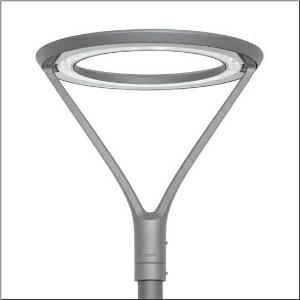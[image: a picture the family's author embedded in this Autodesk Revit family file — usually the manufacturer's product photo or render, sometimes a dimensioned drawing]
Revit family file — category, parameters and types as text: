
# Revit family: dl_r__20___pl1_2s_5xa512832s008_323f
name_source: partatom
category: Lighting Fixtures
units: mm (PartAtom-declared; Revit-internal decimal feet)

## family parameters
Cut with Voids When Loaded = No
Host = Face
Light Source = No
Part Type = Normal
Room Calculation Point = No
Round Connector Dimension = Use Diameter
Shared = No

## types (1)
- --- (1 x LED, 3050 lm, 30.4 W, 2200K)
    Apparent Load = 30 VA
    CIE Flux Codes = 33 78 99 100 100
    Color Rendering = 70
    Color Temperature = 2200K
    Default Elevation = 1800 mm
    Description = DL® 20, mast luminaire, primary light control with reflector, highly specular, primary optical cover: cover, of toughened safety glass of clear glass with excellent transmission level, light distribution: PL1.2s, light emission: direct distribution, primary light characteristic: symmetric, installation type: post-top, LED, High Power LED, rated luminous flux: 3.040lm, luminous efficacy: 86lm/W, light colour: 722, colour temperature: 2200K, control gear: Plus, control: flexible luminous flux parameterisation, time-dependent luminous flux control, constant luminous flux control, digital communication interface, power reduction, overheat protection, electronic power reduction, mains connection: 230..240V, 50/60Hz, connection cable pre-assembled, cable length: 5m, start of lifetime: 36W, end of service life: 36W, reduction: 17W, luminaire housing, upper part, of cast aluminium, powder-coated, Siteco® metallic grey (DB 702S), diameter: 690mm, height: 690mm, spigot size: 76mm (post-top), mounting height: 4..6m, luminaire housing, of cast aluminium, powder-coated, Siteco® metallic grey (DB 702S), equipment: standard, protection rating (complete): IP66, insulation class (complete): insulation class II (safety insulation), certification: CE, ENEC, VDE, impact resistance: IK08, permissible operating ambient temperature: -25..+35°C, standard-compliant lighting for roads and squares, packaging unit: 1 piece

Light Distribution: PL1.2s
    Height = 690 mm
    Lamp = 1 x LED
    Lamp Light Flux = 3050 lm
    Lamp Power = 30.4 W
    Lamp count = 1
    Length = 690 mm
    Luminous efficacy = 100 lm/W
    Manufacturer = Siteco
    ModVariant = No
    Model = 5XA512832S008
    Number of Poles = 1
    OnlyDefault = Yes
    Power Factor = 1
    Product Name = DL® 20 | PL1.2s
    Product group = mast luminaire | pylon top
    ProductGroupID = 6100
    Protection Class = Protection class II
    Protection Degree = IP 66
    RLX_Detail_Level = 1
    RLX_Emergency_Light_Flux = 0 lm
    RLX_Emergency_Type = 0
    RLX_Emergency_Type_DB = No
    RlxData = <blob elided: 204237 chars, md5=9005f40d>
    Socket = socket
    Standby Power = 0 W
    System Light Flux = 3050 lm
    System Power = 30 W
    Type Comments = factory setting: luminous flux: 100 % | dim-lin: 254 | 412 mA
    Type Image = l_1006001.jpg
    URL = http://relux.com
    VarID = @adj_098531
    Voltage = 0 V
    Weight = 0.00 kg
    Width = 0 mm  [stored 0 ft]

note: [stored X ft] marks values corroborated as IEEE doubles in the binary element streams (Revit-internal decimal feet)

## geometry (parser evidence)
native form markers: Blend x4, Sweep x10
no freeform markers — native parametric forms only
